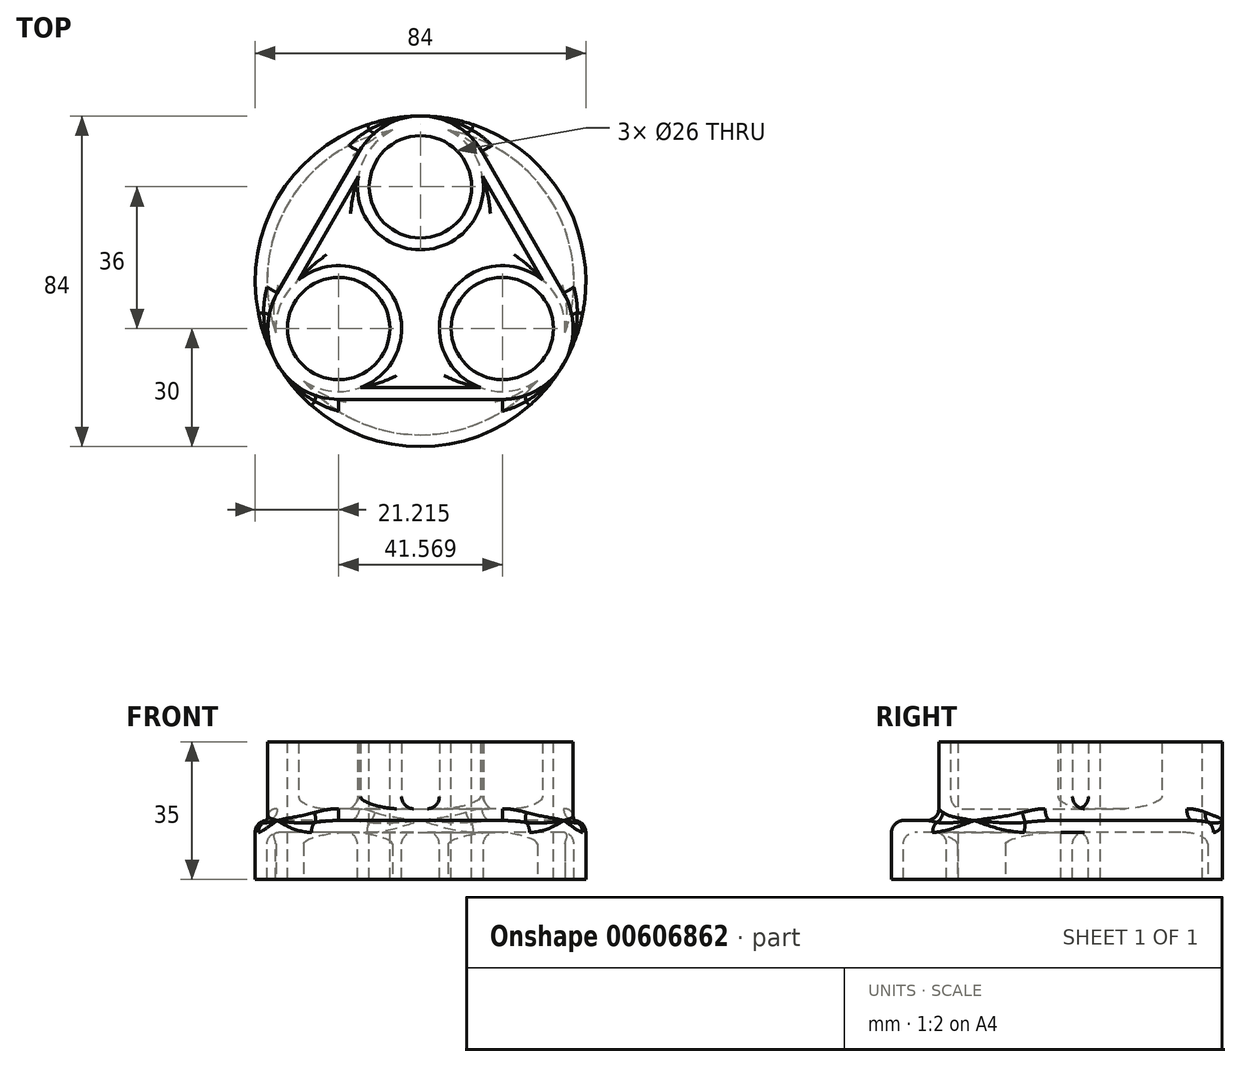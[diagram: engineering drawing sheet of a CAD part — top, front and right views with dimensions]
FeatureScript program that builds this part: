
annotation { "Feature Type Name" : "Feature", "Feature Type Description" : "" }
export const myFeature = defineFeature(function(context is Context, id is Id, definition is map)
    precondition{}
    {
        {
            var Q0;
            Q0=qCreatedBy(makeId("Top.planeOp"),FACE);
            var sketch = newSketch(context, id + "F0", { "sketchPlane" : qUnion([Q0])});
            skCircle(sketch, "E0", {"center": v(0, 0) * mm, "radius": 42 * mm});
            skCircle(sketch, "E1", {"center": v(0, 24) * mm, "radius": 13 * mm});
            skCircle(sketch, "E2", {"center": v(0, 0) * mm, "radius": 24 * mm, "construction": true});
            skCircle(sketch, "E3", {"center": v(0, 24) * mm, "radius": 18 * mm});
            skCircle(sketch, "E4.1.0", {"center": v(-20.78, -12) * mm, "radius": 18 * mm});
            skCircle(sketch, "E4.1.1", {"center": v(-20.78, -12) * mm, "radius": 13 * mm});
            skCircle(sketch, "E4.2.0", {"center": v(20.78, -12) * mm, "radius": 18 * mm});
            skCircle(sketch, "E4.2.1", {"center": v(20.78, -12) * mm, "radius": 13 * mm});
            skLineSegment(sketch, "E5", {"start": v(-15.59, 33) * mm, "end": v(-36.37, -3) * mm});
            skLineSegment(sketch, "E6", {"start": v(-20.78, -30) * mm, "end": v(20.78, -30) * mm});
            skLineSegment(sketch, "E7", {"start": v(36.37, -3) * mm, "end": v(15.59, 33) * mm});
            skSolve(sketch);
        }
        {
            var Q0;
            Q0=makeQuery(id+"F0.imprint","IMPRINT",FACE,{"disambiguationData":[TD([[makeQuery(id+"F0.imprint","IMPRINT",EDGE,{"derivedFrom":sQuery(id+"F0.wireOp",EDGE,"E0")}),1.0]])]});
            var Q1;
            Q1=makeQuery(id+"F0.imprint","IMPRINT",FACE,{"disambiguationData":[TD([[makeQuery(id+"F0.imprint","IMPRINT",EDGE,{"derivedFrom":sQuery(id+"F0.wireOp",EDGE,"E4.1.1")}),-1.0]])]});
            var Q2;
            Q2=makeQuery(id+"F0.imprint","IMPRINT",FACE,{"disambiguationData":[TD([[makeQuery(id+"F0.imprint","IMPRINT",EDGE,{"derivedFrom":sQuery(id+"F0.wireOp",EDGE,"E4.2.1")}),-1.0]])]});
            var Q3;
            Q3=makeQuery(id+"F0.imprint","IMPRINT",FACE,{"disambiguationData":[TD([[makeQuery(id+"F0.imprint","IMPRINT",EDGE,{"derivedFrom":sQuery(id+"F0.wireOp",EDGE,"E1")}),-1.0]])]});
            var Q4;
            {var subQ0=sQuery(id+"F0.wireOp",EDGE,"E5");Q4=makeQuery(id+"F0.imprint","IMPRINT",FACE,{"disambiguationData":[TD([[makeQuery(id+"F0.imprint","IMPRINT",EDGE,{"derivedFrom":subQ0}),1.0]])]});}
            extrude(context, id + "F1", {"entities" : qUnion([Q0, Q1, Q2, Q3, Q4]), "oppositeDirection" : true, "depth" : 15 * mm, "offsetDistance" : 25 * mm});
        }
        {
            var Q0;
            Q0=makeQuery(id+"F1.opExtrude","CAP_FACE",FACE,{"disambiguationData":[OSD([sQuery(id+"F0.wireOp",EDGE,"E0"),sQuery(id+"F0.wireOp",EDGE,"E1"),sQuery(id+"F0.wireOp",EDGE,"E4.1.1"),sQuery(id+"F0.wireOp",EDGE,"E4.2.1")])],"isStart":false});
            shell(context, id + "F2", {"entities" : qUnion([Q0]), "thickness" : 3 * mm});
        }
        {
            var Q0;
            Q0=makeQuery(id+"F0.imprint","IMPRINT",FACE,{"disambiguationData":[TD([[makeQuery(id+"F0.imprint","IMPRINT",EDGE,{"derivedFrom":sQuery(id+"F0.wireOp",EDGE,"E1")}),-1.0]])]});
            var Q1;
            Q1=makeQuery(id+"F0.imprint","IMPRINT",FACE,{"disambiguationData":[TD([[makeQuery(id+"F0.imprint","IMPRINT",EDGE,{"derivedFrom":sQuery(id+"F0.wireOp",EDGE,"E4.1.1")}),-1.0]])]});
            var Q2;
            Q2=makeQuery(id+"F0.imprint","IMPRINT",FACE,{"disambiguationData":[TD([[makeQuery(id+"F0.imprint","IMPRINT",EDGE,{"derivedFrom":sQuery(id+"F0.wireOp",EDGE,"E4.2.1")}),-1.0]])]});
            var Q3;
            {var subQ0=sQuery(id+"F0.wireOp",EDGE,"E5");Q3=makeQuery(id+"F0.imprint","IMPRINT",FACE,{"disambiguationData":[TD([[makeQuery(id+"F0.imprint","IMPRINT",EDGE,{"derivedFrom":subQ0}),1.0]])]});}
            extrude(context, id + "F3", {"entities" : qUnion([Q0, Q1, Q2, Q3]), "depth" : 20 * mm, "offsetDistance" : 25 * mm});
        }
        {
            var Q0;
            Q0=makeQuery(id+"F3.opExtrude","CAP_FACE",FACE,{"disambiguationData":[OSD([sQuery(id+"F0.wireOp",EDGE,"E1"),sQuery(id+"F0.wireOp",EDGE,"E3"),sQuery(id+"F0.wireOp",EDGE,"E4.1.0"),sQuery(id+"F0.wireOp",EDGE,"E4.1.1"),sQuery(id+"F0.wireOp",EDGE,"E4.2.0"),sQuery(id+"F0.wireOp",EDGE,"E4.2.1"),sQuery(id+"F0.wireOp",EDGE,"E5"),sQuery(id+"F0.wireOp",EDGE,"E6"),sQuery(id+"F0.wireOp",EDGE,"E7")])],"isStart":false});
            shell(context, id + "F4", {"entities" : qUnion([Q0]), "thickness" : 3 * mm});
        }
        {
            var Q0;
            Q0=makeQuery(id+"F1.opExtrude","SWEPT_BODY",BODY,{"disambiguationData":[OSD([sQuery(id+"F0.wireOp",EDGE,"E0"),sQuery(id+"F0.wireOp",EDGE,"E1"),sQuery(id+"F0.wireOp",EDGE,"E4.1.1"),sQuery(id+"F0.wireOp",EDGE,"E4.2.1")])]});
            var Q1;
            Q1=makeQuery(id+"F3.opExtrude","SWEPT_BODY",BODY,{"disambiguationData":[OSD([sQuery(id+"F0.wireOp",EDGE,"E1"),sQuery(id+"F0.wireOp",EDGE,"E3"),sQuery(id+"F0.wireOp",EDGE,"E4.1.0"),sQuery(id+"F0.wireOp",EDGE,"E4.1.1"),sQuery(id+"F0.wireOp",EDGE,"E4.2.0"),sQuery(id+"F0.wireOp",EDGE,"E4.2.1"),sQuery(id+"F0.wireOp",EDGE,"E5"),sQuery(id+"F0.wireOp",EDGE,"E6"),sQuery(id+"F0.wireOp",EDGE,"E7")])]});
            booleanBodies(context, id + "F5", {"operationType" : BooleanOperationType.UNION, "tools" : qUnion([Q0, Q1])});
        }
        {
            var Q0;
            {var subQ0=sQuery(id+"F0.wireOp",EDGE,"E0");Q0=makeQuery(id+"F5.opBoolean","SPLIT",EDGE,{"disambiguationData":[TD([makeQuery(id+"F1.opExtrude","SWEPT_FACE",FACE,{"disambiguationData":[OSD([subQ0])]}),makeQuery(id+"F1.opExtrude","CAP_FACE",FACE,{"disambiguationData":[OSD([subQ0,sQuery(id+"F0.wireOp",EDGE,"E1"),sQuery(id+"F0.wireOp",EDGE,"E4.1.1"),sQuery(id+"F0.wireOp",EDGE,"E4.2.1")])],"isStart":true}),makeQuery(id+"F3.opExtrude","SWEPT_FACE",FACE,{"disambiguationData":[OSD([sQuery(id+"F0.wireOp",EDGE,"E4.1.0")])]}),makeQuery(id+"F3.opExtrude","SWEPT_FACE",FACE,{"disambiguationData":[OSD([sQuery(id+"F0.wireOp",EDGE,"E4.2.0")])]})])],"derivedFrom":makeQuery(id+"F1.opExtrude","CAP_EDGE",EDGE,{"disambiguationData":[OSD([subQ0])],"isStart":true})});}
            fillet(context, id + "F6", {"entities" : qUnion([Q0]), "radius" : 3 * mm, "tangentPropagation" : true, "allowEdgeOverflow" : false});
        }
        {
            var Q0;
            Q0=makeQuery(id+"F3.opExtrude","CAP_EDGE",EDGE,{"disambiguationData":[OSD([sQuery(id+"F0.wireOp",EDGE,"E6")])],"isStart":true});
            var Q1;
            Q1=makeQuery(id+"F3.opExtrude","CAP_EDGE",EDGE,{"disambiguationData":[OSD([sQuery(id+"F0.wireOp",EDGE,"E7")])],"isStart":true});
            var Q2;
            Q2=makeQuery(id+"F3.opExtrude","CAP_EDGE",EDGE,{"disambiguationData":[OSD([sQuery(id+"F0.wireOp",EDGE,"E5")])],"isStart":true});
            var Q3;
            Q3=makeQuery(id+"F4.opShell","OFFSET_FACE",FACE,{"disambiguationData":[OSD([sQuery(id+"F0.wireOp",EDGE,"E1"),sQuery(id+"F0.wireOp",EDGE,"E3"),sQuery(id+"F0.wireOp",EDGE,"E4.1.0"),sQuery(id+"F0.wireOp",EDGE,"E4.1.1"),sQuery(id+"F0.wireOp",EDGE,"E4.2.0"),sQuery(id+"F0.wireOp",EDGE,"E4.2.1"),sQuery(id+"F0.wireOp",EDGE,"E5"),sQuery(id+"F0.wireOp",EDGE,"E6"),sQuery(id+"F0.wireOp",EDGE,"E7")])]});
            var Q4;
            Q4=makeQuery(id+"F2.opShell","OFFSET_FACE",FACE,{"disambiguationData":[OSD([sQuery(id+"F0.wireOp",EDGE,"E0"),sQuery(id+"F0.wireOp",EDGE,"E1"),sQuery(id+"F0.wireOp",EDGE,"E4.1.1"),sQuery(id+"F0.wireOp",EDGE,"E4.2.1")])]});
            fillet(context, id + "F7", {"entities" : qUnion([Q0, Q1, Q2, Q3, Q4]), "radius" : 3 * mm, "tangentPropagation" : true, "allowEdgeOverflow" : false});
        }
    });
